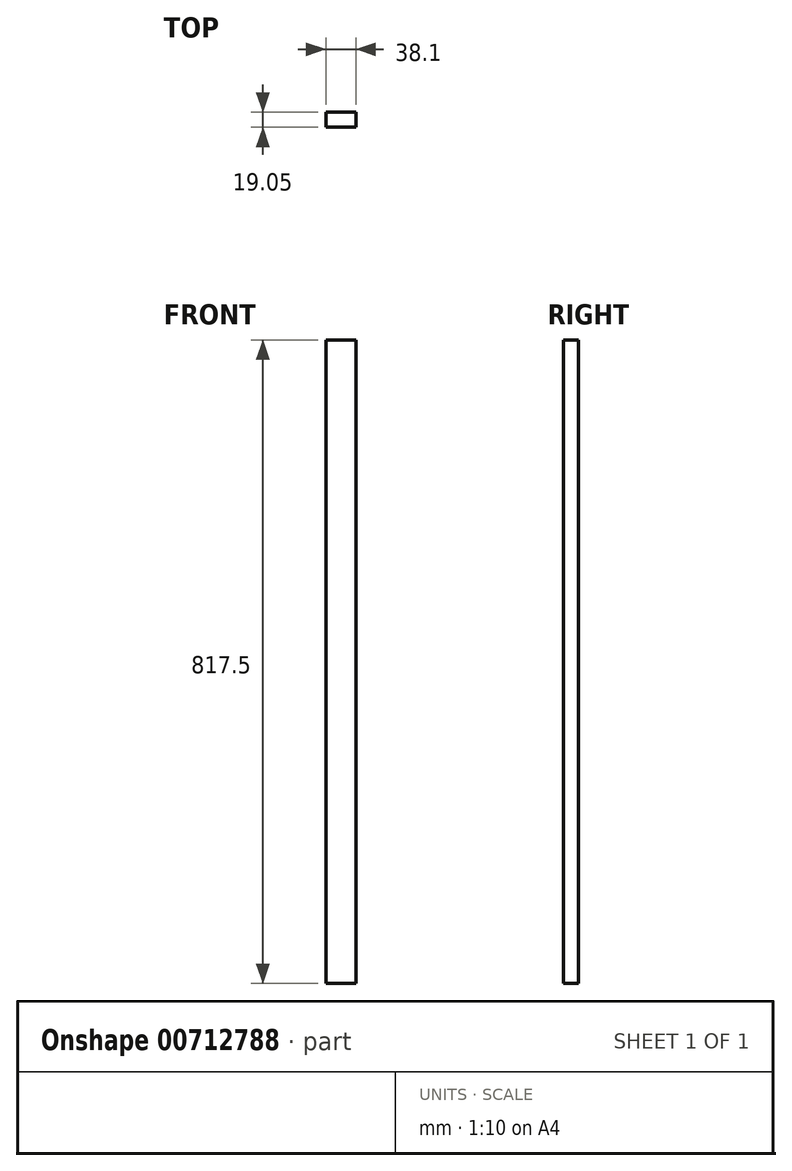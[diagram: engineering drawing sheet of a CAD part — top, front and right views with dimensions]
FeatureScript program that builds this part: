
annotation { "Feature Type Name" : "Feature", "Feature Type Description" : "" }
export const myFeature = defineFeature(function(context is Context, id is Id, definition is map)
    precondition{}
    {
        {
            var Q0;
            Q0=qCreatedBy(makeId("Top.planeOp"),FACE);
            var sketch = newSketch(context, id + "F0", { "sketchPlane" : qUnion([Q0])});
            skLineSegment(sketch, "E0.bottom", {"start": v(0, 0) * mm, "end": v(-38.1, 0) * mm});
            skLineSegment(sketch, "E0.top", {"start": v(0, 19.05) * mm, "end": v(-38.1, 19.05) * mm});
            skLineSegment(sketch, "E0.left", {"start": v(0, 0) * mm, "end": v(0, 19.05) * mm});
            skLineSegment(sketch, "E0.right", {"start": v(-38.1, 0) * mm, "end": v(-38.1, 19.05) * mm});
            skSolve(sketch);
        }
        {
            var Q0;
            Q0 = qSketchRegion(id + "F0", true);
            extrude(context, id + "F1", {"entities" : qUnion([Q0]), "depth" : 817.5 * mm, "offsetDistance" : 25.4 * mm});
        }
    });
